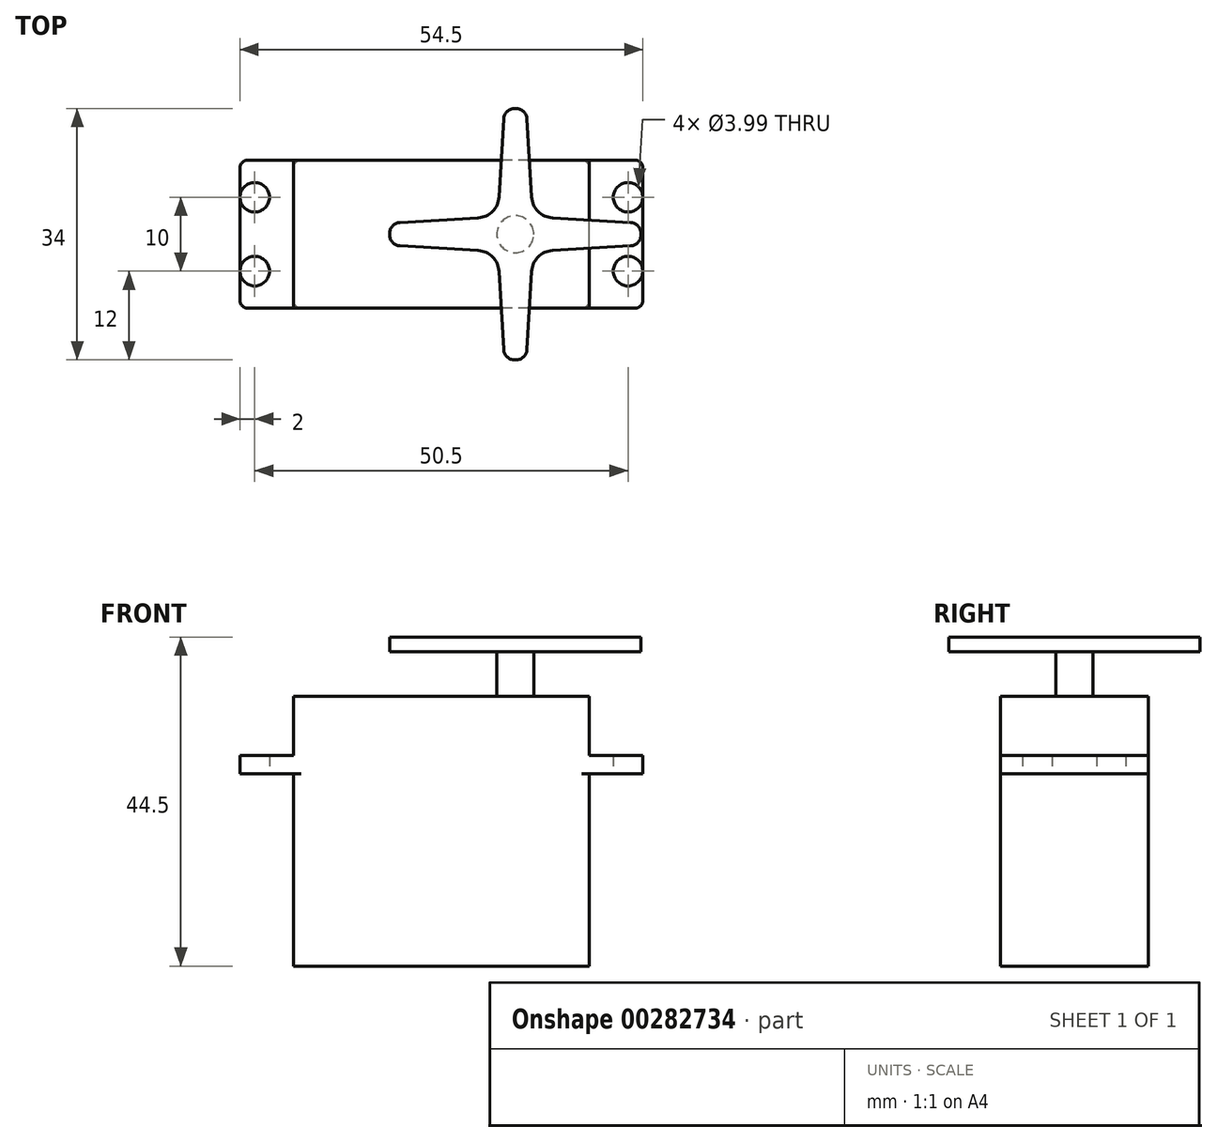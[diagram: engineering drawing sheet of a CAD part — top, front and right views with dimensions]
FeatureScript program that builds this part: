
annotation { "Feature Type Name" : "Feature", "Feature Type Description" : "" }
export const myFeature = defineFeature(function(context is Context, id is Id, definition is map)
    precondition{}
    {
        {
            var Q0;
            Q0=qCreatedBy(makeId("Top.planeOp"),FACE);
            var sketch = newSketch(context, id + "F0", { "sketchPlane" : qUnion([Q0])});
            skLineSegment(sketch, "E0", {"start": v(-74.17, 0) * mm, "end": v(76.51, 0) * mm, "construction": true});
            skLineSegment(sketch, "E1", {"start": v(0, 74.75) * mm, "end": v(0, -75.53) * mm, "construction": true});
            skLineSegment(sketch, "E2.bottom", {"start": v(19, -10) * mm, "end": v(-19, -10) * mm});
            skLineSegment(sketch, "E2.top", {"start": v(19, 10) * mm, "end": v(-19, 10) * mm});
            skLineSegment(sketch, "E2.left", {"start": v(20, -9) * mm, "end": v(20, 9) * mm});
            skLineSegment(sketch, "E2.right", {"start": v(-20, -9) * mm, "end": v(-20, 9) * mm});
            skPoint(sketch, "E2.middle", {"position": v(0, 0) * mm});
            skPoint(sketch, "E3.visualSharp", {"position": v(-20, 10) * mm});
            skArc(sketch, "E3.filletArc", {"start": v(-19, 10) * mm, "mid": v(-19.7, 9.7) * mm, "end": v(-20, 9) * mm});
            skPoint(sketch, "E4.visualSharp", {"position": v(20, 10) * mm});
            skArc(sketch, "E4.filletArc", {"start": v(20, 9) * mm, "mid": v(19.7, 9.7) * mm, "end": v(19, 10) * mm});
            skPoint(sketch, "E5.visualSharp", {"position": v(20, -10) * mm});
            skArc(sketch, "E5.filletArc", {"start": v(19, -10) * mm, "mid": v(19.7, -9.7) * mm, "end": v(20, -9) * mm});
            skPoint(sketch, "E6.visualSharp", {"position": v(-20, -10) * mm});
            skArc(sketch, "E6.filletArc", {"start": v(-20, -9) * mm, "mid": v(-19.7, -9.7) * mm, "end": v(-19, -10) * mm});
            skSolve(sketch);
        }
        {
            var Q0;
            Q0=qSketchRegion(id+"F0",true);
            extrude(context, id + "F1", {"entities" : qUnion([Q0]), "depth" : 26 * mm});
        }
        {
            var Q0;
            Q0=makeQuery(id+"F1.opExtrude","CAP_FACE",FACE,{"disambiguationData":[OSD([sQuery(id+"F0.wireOp",EDGE,"E2.bottom"),sQuery(id+"F0.wireOp",EDGE,"E2.top"),sQuery(id+"F0.wireOp",EDGE,"E2.left"),sQuery(id+"F0.wireOp",EDGE,"E2.right"),sQuery(id+"F0.wireOp",EDGE,"E3.filletArc"),sQuery(id+"F0.wireOp",EDGE,"E4.filletArc"),sQuery(id+"F0.wireOp",EDGE,"E5.filletArc"),sQuery(id+"F0.wireOp",EDGE,"E6.filletArc")])],"isStart":false});
            var sketch = newSketch(context, id + "F2", { "sketchPlane" : qUnion([Q0])});
            skLineSegment(sketch, "E7", {"start": v(-69.92, 0) * mm, "end": v(54, 0) * mm, "construction": true});
            skPoint(sketch, "E7.startSnap0", {"position": v(-20, 0) * mm});
            skLineSegment(sketch, "E8", {"start": v(0, 31.92) * mm, "end": v(0, -23.22) * mm, "construction": true});
            skLineSegment(sketch, "E9.bottom", {"start": v(26.25, -10) * mm, "end": v(-26.25, -10) * mm});
            skLineSegment(sketch, "E9.top", {"start": v(26.25, 10) * mm, "end": v(-26.25, 10) * mm});
            skLineSegment(sketch, "E9.left", {"start": v(27.25, -9) * mm, "end": v(27.25, 9) * mm});
            skLineSegment(sketch, "E9.right", {"start": v(-27.25, -9) * mm, "end": v(-27.25, 9) * mm});
            skPoint(sketch, "E9.middle", {"position": v(0, 0) * mm});
            skLineSegment(sketch, "E10", {"start": v(-25.25, 12.88) * mm, "end": v(-25.25, -17.15) * mm, "construction": true});
            skPoint(sketch, "E11", {"position": v(-25.25, 5) * mm});
            skPoint(sketch, "E12", {"position": v(-25.25, -5) * mm});
            skPoint(sketch, "E13.MirrorP", {"position": v(25.25, 5) * mm});
            skPoint(sketch, "E14.MirrorP", {"position": v(25.25, -5) * mm});
            skPoint(sketch, "E15.visualSharp", {"position": v(-27.25, 10) * mm});
            skArc(sketch, "E15.filletArc", {"start": v(-26.25, 10) * mm, "mid": v(-26.96, 9.7) * mm, "end": v(-27.25, 9) * mm});
            skPoint(sketch, "E16.visualSharp", {"position": v(-27.25, -10) * mm});
            skArc(sketch, "E16.filletArc", {"start": v(-27.25, -9) * mm, "mid": v(-26.96, -9.7) * mm, "end": v(-26.25, -10) * mm});
            skPoint(sketch, "E17.visualSharp", {"position": v(27.25, 10) * mm});
            skArc(sketch, "E17.filletArc", {"start": v(27.25, 9) * mm, "mid": v(26.96, 9.7) * mm, "end": v(26.25, 10) * mm});
            skPoint(sketch, "E18.visualSharp", {"position": v(27.25, -10) * mm});
            skArc(sketch, "E18.filletArc", {"start": v(26.25, -10) * mm, "mid": v(26.96, -9.7) * mm, "end": v(27.25, -9) * mm});
            skSolve(sketch);
        }
        {
            var Q0;
            Q0=qSketchRegion(id+"F2",true);
            extrude(context, id + "F3", {"entities" : qUnion([Q0]), "operationType" : NewBodyOperationType.ADD, "depth" : 2.5 * mm});
        }
        {
            var Q0;
            Q0=sQuery(id+"F2.wireOp",VERTEX,"E11");
            var Q1;
            Q1=sQuery(id+"F2.wireOp",VERTEX,"E12");
            var Q2;
            Q2=sQuery(id+"F2.wireOp",VERTEX,"E13.MirrorP");
            var Q3;
            Q3=sQuery(id+"F2.wireOp",VERTEX,"E14.MirrorP");
            var Q4;
            Q4=makeQuery(id+"F1.opExtrude","SWEPT_BODY",BODY,{"disambiguationData":[OSD([sQuery(id+"F0.wireOp",EDGE,"E2.bottom"),sQuery(id+"F0.wireOp",EDGE,"E2.top"),sQuery(id+"F0.wireOp",EDGE,"E2.left"),sQuery(id+"F0.wireOp",EDGE,"E2.right"),sQuery(id+"F0.wireOp",EDGE,"E3.filletArc"),sQuery(id+"F0.wireOp",EDGE,"E4.filletArc"),sQuery(id+"F0.wireOp",EDGE,"E5.filletArc"),sQuery(id+"F0.wireOp",EDGE,"E6.filletArc")])]});
            hole(context, id + "F4", {"style" : HoleStyle.SIMPLE, "endStyle" : HoleEndStyle.BLIND, "oppositeDirection" : true, "holeDiameter" : 4 * mm, "holeDepth" : 5 * mm, "tappedDepth" : 12 * mm, "tapClearance" : 3, "startFromSketch" : true, "locations" : qUnion([Q0, Q1, Q2, Q3]), "scope" : qUnion([Q4])});
        }
        {
            var Q0;
            Q0=makeQuery(id+"F3.opExtrude","CAP_FACE",FACE,{"disambiguationData":[OSD([sQuery(id+"F2.wireOp",EDGE,"E9.bottom"),sQuery(id+"F2.wireOp",EDGE,"E9.top"),sQuery(id+"F2.wireOp",EDGE,"E9.left"),sQuery(id+"F2.wireOp",EDGE,"E9.right"),sQuery(id+"F2.wireOp",EDGE,"E15.filletArc"),sQuery(id+"F2.wireOp",EDGE,"E16.filletArc"),sQuery(id+"F2.wireOp",EDGE,"E17.filletArc"),sQuery(id+"F2.wireOp",EDGE,"E18.filletArc")])],"isStart":false});
            var sketch = newSketch(context, id + "F5", { "sketchPlane" : qUnion([Q0])});
            skLineSegment(sketch, "E19.bottom", {"start": v(20, -10) * mm, "end": v(-20, -10) * mm});
            skLineSegment(sketch, "E19.top", {"start": v(20, 10) * mm, "end": v(-20, 10) * mm});
            skLineSegment(sketch, "E19.left", {"start": v(20, -10) * mm, "end": v(20, 10) * mm});
            skLineSegment(sketch, "E19.right", {"start": v(-20, -10) * mm, "end": v(-20, 10) * mm});
            skPoint(sketch, "E19.middle", {"position": v(0, 0) * mm});
            skSolve(sketch);
        }
        {
            var Q0;
            Q0=qSketchRegion(id+"F5",true);
            extrude(context, id + "F6", {"entities" : qUnion([Q0]), "operationType" : NewBodyOperationType.ADD, "depth" : 8 * mm});
        }
        {
            var Q0;
            Q0=makeQuery(id+"F6.opExtrude","CAP_FACE",FACE,{"disambiguationData":[OSD([sQuery(id+"F5.wireOp",EDGE,"E19.bottom"),sQuery(id+"F5.wireOp",EDGE,"E19.top"),sQuery(id+"F5.wireOp",EDGE,"E19.left"),sQuery(id+"F5.wireOp",EDGE,"E19.right")])],"isStart":false});
            var sketch = newSketch(context, id + "F7", { "sketchPlane" : qUnion([Q0])});
            skLineSegment(sketch, "E20", {"start": v(-27.08, 0) * mm, "end": v(27.57, 0) * mm, "construction": true});
            skPoint(sketch, "E20.startSnap0", {"position": v(-20, 0) * mm});
            skPoint(sketch, "E20.endSnap0", {"position": v(20, 0) * mm});
            skLineSegment(sketch, "E21", {"start": v(0, 10) * mm, "end": v(0, -10) * mm, "construction": true});
            skLineSegment(sketch, "E22", {"start": v(10, 10) * mm, "end": v(10, -10) * mm, "construction": true});
            skPoint(sketch, "E23", {"position": v(10, 0) * mm});
            skCircle(sketch, "E24", {"center": v(10, 0) * mm, "radius": 2.5 * mm});
            skLineSegment(sketch, "E25", {"start": v(30, 0.07) * mm, "end": v(30, -0.07) * mm});
            skLineSegment(sketch, "E26", {"start": v(28.57, 1.57) * mm, "end": v(13.29, 2.34) * mm});
            skLineSegment(sketch, "E27", {"start": v(28.58, -1.57) * mm, "end": v(13.28, -2.34) * mm});
            skPoint(sketch, "E28.visualSharp", {"position": v(30, 1.5) * mm});
            skArc(sketch, "E28.filletArc", {"start": v(30, 0.07) * mm, "mid": v(29.59, 1.1) * mm, "end": v(28.57, 1.57) * mm});
            skPoint(sketch, "E29.visualSharp", {"position": v(30, -1.5) * mm});
            skArc(sketch, "E29.filletArc", {"start": v(28.58, -1.57) * mm, "mid": v(29.59, -1.1) * mm, "end": v(30, -0.07) * mm});
            skLineSegment(sketch, "E30.1.0", {"start": v(8.43, 18.57) * mm, "end": v(7.66, 3.29) * mm});
            skPoint(sketch, "E30.1.1", {"position": v(8.5, 20) * mm});
            skArc(sketch, "E30.1.2", {"start": v(9.93, 20) * mm, "mid": v(8.9, 19.59) * mm, "end": v(8.43, 18.57) * mm});
            skArc(sketch, "E30.1.3", {"start": v(11.57, 18.58) * mm, "mid": v(11.1, 19.59) * mm, "end": v(10.07, 20) * mm});
            skLineSegment(sketch, "E30.1.4", {"start": v(11.57, 18.58) * mm, "end": v(12.34, 3.28) * mm});
            skLineSegment(sketch, "E30.2.0", {"start": v(-8.57, -1.57) * mm, "end": v(6.71, -2.34) * mm});
            skPoint(sketch, "E30.2.1", {"position": v(-10, -1.5) * mm});
            skArc(sketch, "E30.2.2", {"start": v(-10, -0.07) * mm, "mid": v(-9.59, -1.1) * mm, "end": v(-8.57, -1.57) * mm});
            skArc(sketch, "E30.2.3", {"start": v(-8.58, 1.57) * mm, "mid": v(-9.59, 1.1) * mm, "end": v(-10, 0.07) * mm});
            skLineSegment(sketch, "E30.2.4", {"start": v(-8.58, 1.57) * mm, "end": v(6.72, 2.34) * mm});
            skLineSegment(sketch, "E30.3.0", {"start": v(11.57, -18.57) * mm, "end": v(12.34, -3.29) * mm});
            skPoint(sketch, "E30.3.1", {"position": v(11.5, -20) * mm});
            skArc(sketch, "E30.3.2", {"start": v(10.07, -20) * mm, "mid": v(11.1, -19.59) * mm, "end": v(11.57, -18.57) * mm});
            skArc(sketch, "E30.3.3", {"start": v(8.43, -18.58) * mm, "mid": v(8.9, -19.59) * mm, "end": v(9.93, -20) * mm});
            skLineSegment(sketch, "E30.3.4", {"start": v(8.43, -18.58) * mm, "end": v(7.66, -3.28) * mm});
            skPoint(sketch, "E31.newPointA", {"position": v(12.5, 0.13) * mm});
            skPoint(sketch, "E31.newPointB", {"position": v(10, 2.5) * mm});
            skArc(sketch, "E31.filletArc", {"start": v(12.34, 3.28) * mm, "mid": v(12.63, 2.63) * mm, "end": v(13.29, 2.34) * mm});
            skPoint(sketch, "E32.newPointA", {"position": v(12.5, 0) * mm});
            skPoint(sketch, "E32.newPointB", {"position": v(10.13, -2.5) * mm});
            skArc(sketch, "E32.filletArc", {"start": v(13.28, -2.34) * mm, "mid": v(12.63, -2.63) * mm, "end": v(12.34, -3.29) * mm});
            skPoint(sketch, "E33.newPointA", {"position": v(10, -2.5) * mm});
            skPoint(sketch, "E33.newPointB", {"position": v(7.5, -0.13) * mm});
            skArc(sketch, "E33.filletArc", {"start": v(7.66, -3.28) * mm, "mid": v(7.37, -2.63) * mm, "end": v(6.71, -2.34) * mm});
            skPoint(sketch, "E34.newPointA", {"position": v(9.87, 2.5) * mm});
            skPoint(sketch, "E34.newPointB", {"position": v(7.5, 0) * mm});
            skArc(sketch, "E34.filletArc", {"start": v(6.72, 2.34) * mm, "mid": v(7.37, 2.63) * mm, "end": v(7.66, 3.29) * mm});
            skSolve(sketch);
        }
        {
            var Q0;
            Q0=qSketchRegion(id+"F7",true);
            extrude(context, id + "F8", {"entities" : qUnion([Q0]), "depth" : 6 * mm});
        }
        {
            var Q0;
            Q0=makeQuery(id+"F8.opExtrude","CAP_FACE",FACE,{"disambiguationData":[OSD([sQuery(id+"F7.wireOp",EDGE,"E24")])],"isStart":false});
            var sketch = newSketch(context, id + "F9", { "sketchPlane" : qUnion([Q0])});
            skLineSegment(sketch, "E35", {"start": v(-26.82, 0) * mm, "end": v(26.9, 0) * mm, "construction": true});
            skLineSegment(sketch, "E36", {"start": v(10, 9.8) * mm, "end": v(10, -10.05) * mm, "construction": true});
            skCircle(sketch, "E37", {"center": v(10, 0) * mm, "radius": 2.5 * mm, "construction": true});
            skLineSegment(sketch, "E38", {"start": v(-7, 0.09) * mm, "end": v(-7, -0.09) * mm});
            skLineSegment(sketch, "E39", {"start": v(-5.59, 1.58) * mm, "end": v(4.98, 2.2) * mm});
            skLineSegment(sketch, "E40", {"start": v(-5.59, -1.58) * mm, "end": v(4.97, -2.2) * mm});
            skPoint(sketch, "E41.visualSharp", {"position": v(-7, 1.5) * mm});
            skArc(sketch, "E41.filletArc", {"start": v(-5.59, 1.58) * mm, "mid": v(-6.6, 1.11) * mm, "end": v(-7, 0.09) * mm});
            skPoint(sketch, "E42.visualSharp", {"position": v(-7, -1.5) * mm});
            skArc(sketch, "E42.filletArc", {"start": v(-7, -0.09) * mm, "mid": v(-6.6, -1.11) * mm, "end": v(-5.59, -1.58) * mm});
            skLineSegment(sketch, "E43.1.0", {"start": v(8.42, -15.59) * mm, "end": v(7.8, -5.02) * mm});
            skArc(sketch, "E43.1.1", {"start": v(8.42, -15.59) * mm, "mid": v(8.89, -16.6) * mm, "end": v(9.91, -17) * mm});
            skArc(sketch, "E43.1.2", {"start": v(10.09, -17) * mm, "mid": v(11.11, -16.6) * mm, "end": v(11.58, -15.59) * mm});
            skLineSegment(sketch, "E43.1.3", {"start": v(11.58, -15.59) * mm, "end": v(12.2, -5.03) * mm});
            skLineSegment(sketch, "E43.1.4", {"start": v(9.91, -17) * mm, "end": v(10.09, -17) * mm});
            skLineSegment(sketch, "E43.2.0", {"start": v(25.59, -1.58) * mm, "end": v(15.02, -2.2) * mm});
            skArc(sketch, "E43.2.1", {"start": v(25.59, -1.58) * mm, "mid": v(26.6, -1.11) * mm, "end": v(27, -0.09) * mm});
            skArc(sketch, "E43.2.2", {"start": v(27, 0.09) * mm, "mid": v(26.6, 1.11) * mm, "end": v(25.59, 1.58) * mm});
            skLineSegment(sketch, "E43.2.3", {"start": v(25.59, 1.58) * mm, "end": v(15.03, 2.2) * mm});
            skLineSegment(sketch, "E43.2.4", {"start": v(27, -0.09) * mm, "end": v(27, 0.09) * mm});
            skLineSegment(sketch, "E43.3.0", {"start": v(11.58, 15.59) * mm, "end": v(12.2, 5.02) * mm});
            skArc(sketch, "E43.3.1", {"start": v(11.58, 15.59) * mm, "mid": v(11.11, 16.6) * mm, "end": v(10.09, 17) * mm});
            skArc(sketch, "E43.3.2", {"start": v(9.91, 17) * mm, "mid": v(8.89, 16.6) * mm, "end": v(8.42, 15.59) * mm});
            skLineSegment(sketch, "E43.3.3", {"start": v(8.42, 15.59) * mm, "end": v(7.8, 5.03) * mm});
            skLineSegment(sketch, "E43.3.4", {"start": v(10.09, 17) * mm, "end": v(9.91, 17) * mm});
            skPoint(sketch, "E44.newPointA", {"position": v(9.85, 2.5) * mm});
            skPoint(sketch, "E44.newPointB", {"position": v(7.5, 0) * mm});
            skArc(sketch, "E44.filletArc", {"start": v(4.98, 2.2) * mm, "mid": v(6.92, 3.08) * mm, "end": v(7.8, 5.03) * mm});
            skPoint(sketch, "E45.newPointA", {"position": v(12.5, 0.15) * mm});
            skPoint(sketch, "E45.newPointB", {"position": v(10, 2.5) * mm});
            skArc(sketch, "E45.filletArc", {"start": v(12.2, 5.02) * mm, "mid": v(13.08, 3.08) * mm, "end": v(15.03, 2.2) * mm});
            skPoint(sketch, "E46.newPointA", {"position": v(10.15, -2.5) * mm});
            skPoint(sketch, "E46.newPointB", {"position": v(12.5, 0) * mm});
            skArc(sketch, "E46.filletArc", {"start": v(15.02, -2.2) * mm, "mid": v(13.08, -3.08) * mm, "end": v(12.2, -5.03) * mm});
            skPoint(sketch, "E47.newPointA", {"position": v(10, -2.5) * mm});
            skPoint(sketch, "E47.newPointB", {"position": v(7.5, -0.15) * mm});
            skArc(sketch, "E47.filletArc", {"start": v(7.8, -5.02) * mm, "mid": v(6.92, -3.08) * mm, "end": v(4.97, -2.2) * mm});
            skSolve(sketch);
        }
        {
            var Q0;
            Q0=qSketchRegion(id+"F9",true);
            extrude(context, id + "F10", {"entities" : qUnion([Q0]), "operationType" : NewBodyOperationType.ADD, "depth" : 2 * mm});
        }
    });
